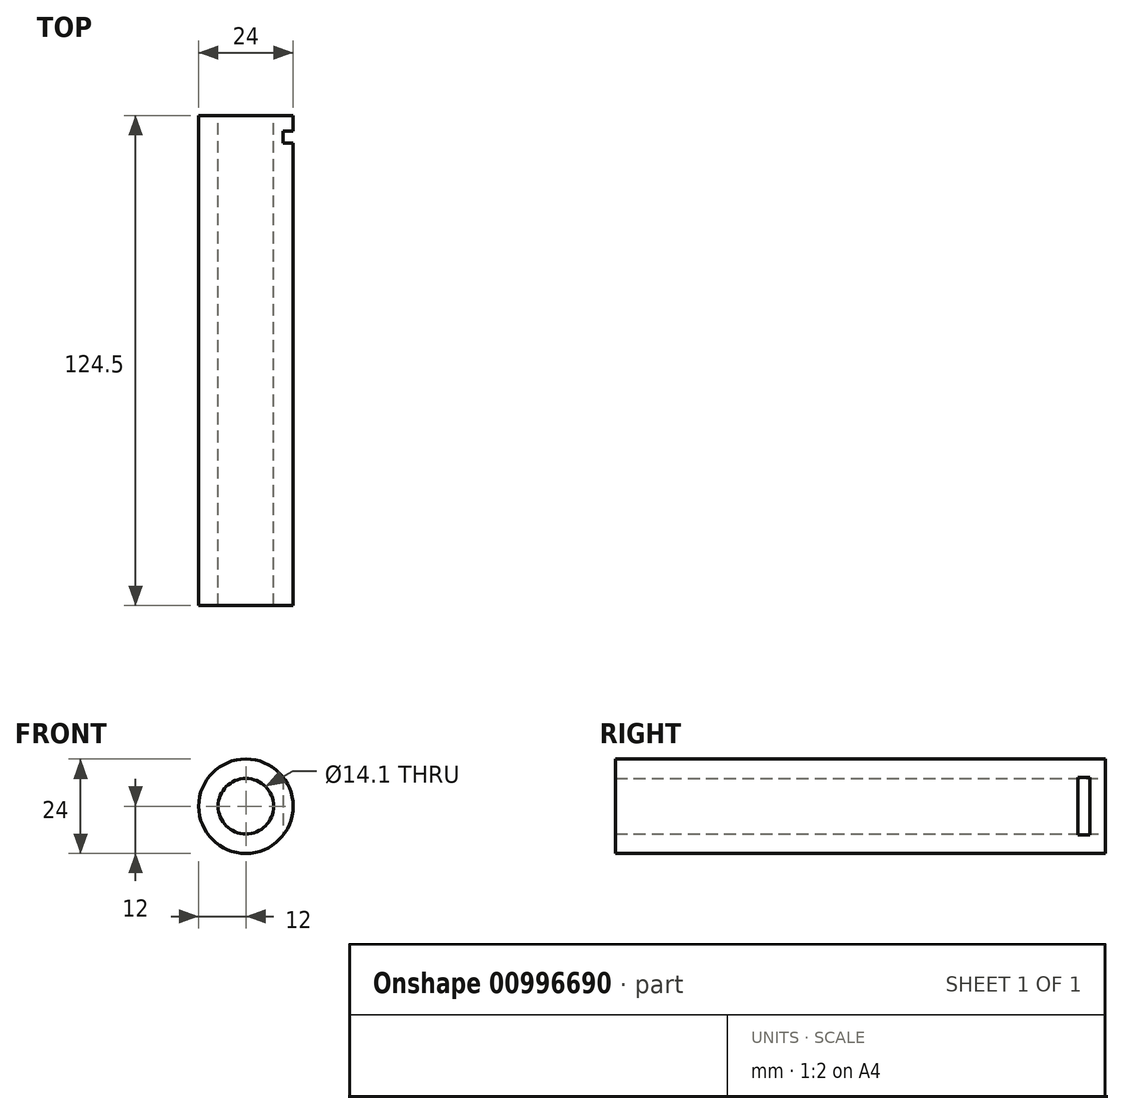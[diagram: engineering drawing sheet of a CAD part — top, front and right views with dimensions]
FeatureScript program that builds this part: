
annotation { "Feature Type Name" : "Feature", "Feature Type Description" : "" }
export const myFeature = defineFeature(function(context is Context, id is Id, definition is map)
    precondition{}
    {
        {
            var Q0;
            Q0=qCreatedBy(makeId("Front.planeOp"),FACE);
            var sketch = newSketch(context, id + "F0", { "sketchPlane" : qUnion([Q0])});
            skLineSegment(sketch, "E0", {"start": v(0, 0) * mm, "end": v(0, -12) * mm, "construction": true});
            skLineSegment(sketch, "E1", {"start": v(0, -12) * mm, "end": v(-12, -12) * mm, "construction": true});
            skCircle(sketch, "E2", {"center": v(-12, -12) * mm, "radius": 12 * mm});
            skCircle(sketch, "E3", {"center": v(-12, -12) * mm, "radius": 7.05 * mm});
            skSolve(sketch);
        }
        {
            var Q0;
            Q0=makeQuery(id+"F0.imprint","IMPRINT",FACE,{"disambiguationData":[TD([[makeQuery(id+"F0.imprint","IMPRINT",EDGE,{"derivedFrom":sQuery(id+"F0.wireOp",EDGE,"E2")}),1.0]])]});
            extrude(context, id + "F1", {"entities" : qUnion([Q0]), "depth" : 124.5 * mm, "offsetDistance" : 25 * mm});
        }
        {
            var Q0;
            Q0=qCreatedBy(makeId("Right.planeOp"),FACE);
            var sketch = newSketch(context, id + "F2", { "sketchPlane" : qUnion([Q0])});
            skLineSegment(sketch, "E4.0", {"start": v(0, -24) * mm, "end": v(0, 0) * mm, "construction": true});
            skLineSegment(sketch, "E5.bottom", {"start": v(-7, 0) * mm, "end": v(-4, 0) * mm});
            skLineSegment(sketch, "E5.top", {"start": v(-7, -24) * mm, "end": v(-4, -24) * mm});
            skLineSegment(sketch, "E5.left", {"start": v(-7, 0) * mm, "end": v(-7, -24) * mm});
            skLineSegment(sketch, "E5.right", {"start": v(-4, 0) * mm, "end": v(-4, -24) * mm});
            skSolve(sketch);
        }
        {
            var Q0;
            Q0=makeQuery(id+"F2.imprint","IMPRINT",FACE,{"disambiguationData":[TD([[makeQuery(id+"F2.imprint","IMPRINT",EDGE,{"derivedFrom":sQuery(id+"F2.wireOp",EDGE,"E5.bottom")}),-1.0]])]});
            extrude(context, id + "F3", {"entities" : qUnion([Q0]), "operationType" : NewBodyOperationType.REMOVE, "oppositeDirection" : true, "depth" : 2.5 * mm, "offsetDistance" : 25 * mm});
        }
    });
